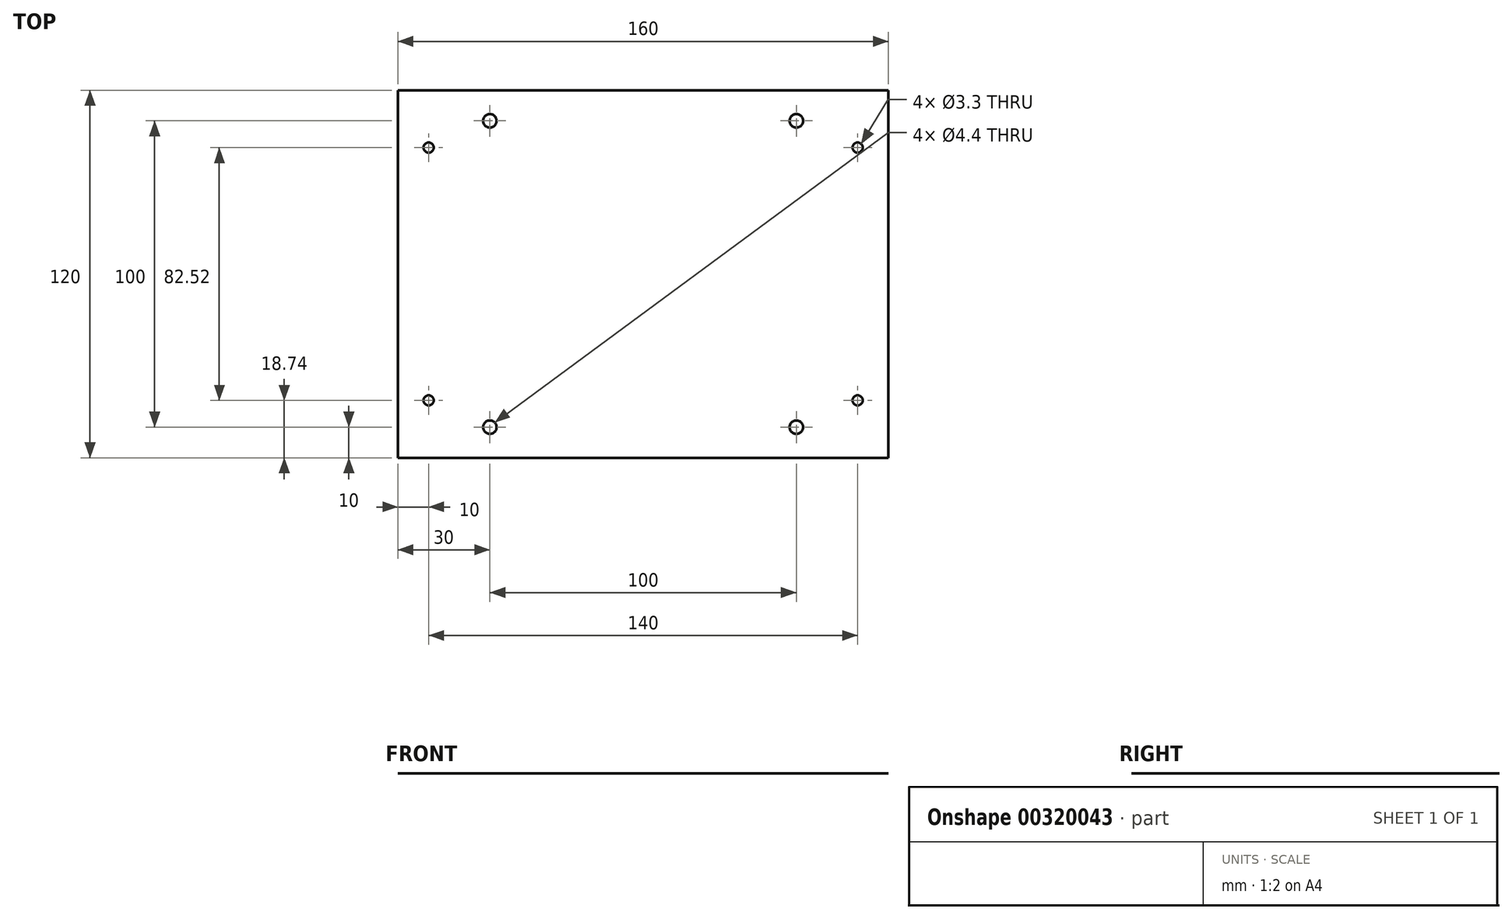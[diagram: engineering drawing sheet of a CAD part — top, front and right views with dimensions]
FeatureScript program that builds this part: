
annotation { "Feature Type Name" : "Feature", "Feature Type Description" : "" }
export const myFeature = defineFeature(function(context is Context, id is Id, definition is map)
    precondition{}
    {
        {
            var Q0;
            Q0=qCreatedBy(makeId("Top.planeOp"),FACE);
            var sketch = newSketch(context, id + "F0", { "sketchPlane" : qUnion([Q0])});
            skLineSegment(sketch, "E0.bottom", {"start": v(-70, 41.26) * mm, "end": v(70, 41.26) * mm, "construction": true});
            skLineSegment(sketch, "E0.top", {"start": v(-70, -41.26) * mm, "end": v(70, -41.26) * mm, "construction": true});
            skLineSegment(sketch, "E0.left", {"start": v(-70, 41.26) * mm, "end": v(-70, -41.26) * mm, "construction": true});
            skLineSegment(sketch, "E0.right", {"start": v(70, 41.26) * mm, "end": v(70, -41.26) * mm, "construction": true});
            skLineSegment(sketch, "E1", {"start": v(0, 41.26) * mm, "end": v(0, -41.26) * mm, "construction": true});
            skLineSegment(sketch, "E2", {"start": v(-70, 0) * mm, "end": v(70, 0) * mm, "construction": true});
            skCircle(sketch, "E3", {"center": v(-70, 41.26) * mm, "radius": 1.65 * mm});
            skCircle(sketch, "E4", {"center": v(70, 41.26) * mm, "radius": 1.65 * mm});
            skCircle(sketch, "E5", {"center": v(-70, -41.26) * mm, "radius": 1.65 * mm});
            skCircle(sketch, "E6", {"center": v(70, -41.26) * mm, "radius": 1.65 * mm});
            skLineSegment(sketch, "E7.bottom", {"start": v(-50, 50) * mm, "end": v(50, 50) * mm, "construction": true});
            skLineSegment(sketch, "E7.top", {"start": v(-50, -50) * mm, "end": v(50, -50) * mm, "construction": true});
            skLineSegment(sketch, "E7.left", {"start": v(-50, 50) * mm, "end": v(-50, -50) * mm, "construction": true});
            skLineSegment(sketch, "E7.right", {"start": v(50, 50) * mm, "end": v(50, -50) * mm, "construction": true});
            skLineSegment(sketch, "E8", {"start": v(0, 41.26) * mm, "end": v(0, 50) * mm, "construction": true});
            skPoint(sketch, "E9.start.orphan", {"position": v(0, -50) * mm});
            skLineSegment(sketch, "E10", {"start": v(-50, 0) * mm, "end": v(-70, 0) * mm, "construction": true});
            skCircle(sketch, "E11", {"center": v(-50, 50) * mm, "radius": 2.2 * mm});
            skCircle(sketch, "E12", {"center": v(50, 50) * mm, "radius": 2.2 * mm});
            skCircle(sketch, "E13", {"center": v(50, -50) * mm, "radius": 2.2 * mm});
            skCircle(sketch, "E14", {"center": v(-50, -50) * mm, "radius": 2.2 * mm});
            skLineSegment(sketch, "E15.bottom", {"start": v(-80, 60) * mm, "end": v(80, 60) * mm});
            skLineSegment(sketch, "E15.top", {"start": v(-80, -60) * mm, "end": v(80, -60) * mm});
            skLineSegment(sketch, "E15.left", {"start": v(-80, 60) * mm, "end": v(-80, -60) * mm});
            skLineSegment(sketch, "E15.right", {"start": v(80, 60) * mm, "end": v(80, -60) * mm});
            skLineSegment(sketch, "E16", {"start": v(-80, 0) * mm, "end": v(-70, 0) * mm, "construction": true});
            skLineSegment(sketch, "E17", {"start": v(0, 60) * mm, "end": v(0, 50) * mm, "construction": true});
            skSolve(sketch);
        }
        {
            var Q0;
            Q0 = qSketchRegion(id + "F0", true);
            extrude(context, id + "F1", {"entities" : qUnion([Q0]), "depth" : 1 / 203.2 * mm});
        }
    });
